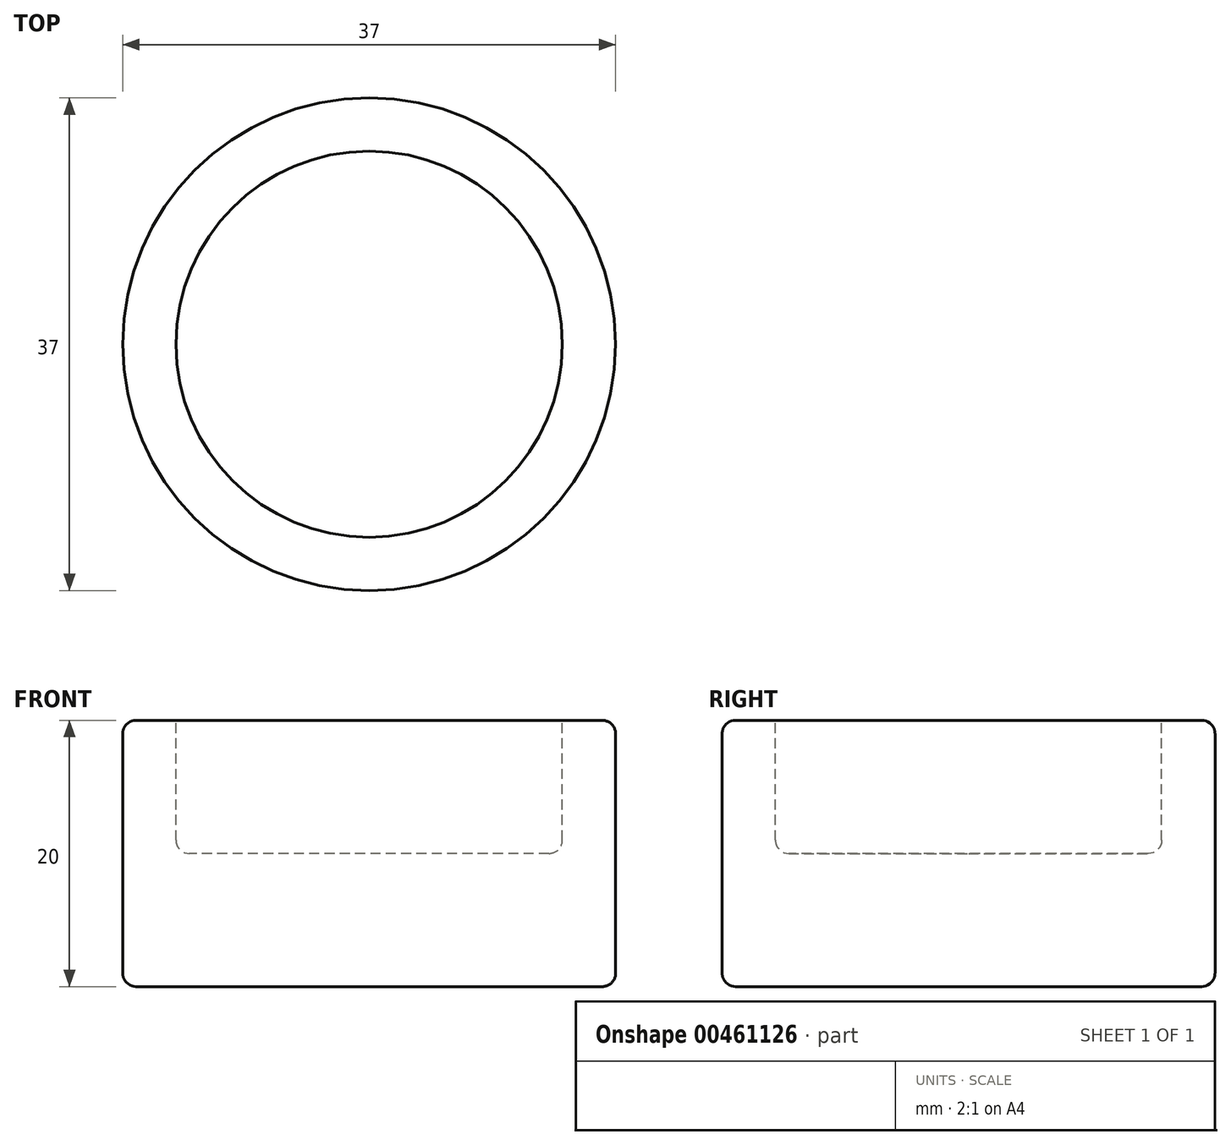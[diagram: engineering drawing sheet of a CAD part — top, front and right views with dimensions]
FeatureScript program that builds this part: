
annotation { "Feature Type Name" : "Feature", "Feature Type Description" : "" }
export const myFeature = defineFeature(function(context is Context, id is Id, definition is map)
    precondition{}
    {
        {
            var Q0;
            Q0=qCreatedBy(makeId("Top.planeOp"),FACE);
            var sketch = newSketch(context, id + "F0", { "sketchPlane" : qUnion([Q0])});
            skCircle(sketch, "E0", {"center": v(0, 0) * mm, "radius": 18.5 * mm});
            skSolve(sketch);
        }
        {
            var Q0;
            Q0 = qSketchRegion(id + "F0", true);
            extrude(context, id + "F1", {"entities" : qUnion([Q0]), "depth" : 20 * mm, "offsetDistance" : 25 * mm});
        }
        {
            var Q0;
            Q0=makeQuery(id+"F1.opExtrude","CAP_FACE",FACE,{"disambiguationData":[OSD([sQuery(id+"F0.wireOp",EDGE,"E0")])],"isStart":false});
            var sketch = newSketch(context, id + "F2", { "sketchPlane" : qUnion([Q0])});
            skCircle(sketch, "E1", {"center": v(0, 0) * mm, "radius": 14.5 * mm});
            skSolve(sketch);
        }
        {
            var Q0;
            Q0 = qSketchRegion(id + "F2", true);
            extrude(context, id + "F3", {"entities" : qUnion([Q0]), "operationType" : NewBodyOperationType.REMOVE, "oppositeDirection" : true, "depth" : 10 * mm, "offsetDistance" : 25 * mm});
        }
        {
            var Q0;
            Q0=makeQuery(id+"F1.opExtrude","CAP_EDGE",EDGE,{"disambiguationData":[OSD([sQuery(id+"F0.wireOp",EDGE,"E0")])],"isStart":false});
            var Q1;
            Q1=makeQuery(id+"F3.boolean.opBoolean","COPY",EDGE,{"derivedFrom":makeQuery(id+"F3.opExtrude","CAP_EDGE",EDGE,{"disambiguationData":[OSD([sQuery(id+"F2.wireOp",EDGE,"E1")])],"isStart":true})});
            var Q2;
            Q2=makeQuery(id+"F1.opExtrude","CAP_EDGE",EDGE,{"disambiguationData":[OSD([sQuery(id+"F0.wireOp",EDGE,"E0")])],"isStart":true});
            var Q3;
            Q3=makeQuery(id+"F3.boolean.opBoolean","COPY",EDGE,{"derivedFrom":makeQuery(id+"F3.opExtrude","CAP_EDGE",EDGE,{"disambiguationData":[OSD([sQuery(id+"F2.wireOp",EDGE,"E1")])],"isStart":false})});
            fillet(context, id + "F4", {"entities" : qUnion([Q0, Q1, Q2, Q3]), "radius" : 1 * mm, "tangentPropagation" : true, "allowEdgeOverflow" : false});
        }
    });
